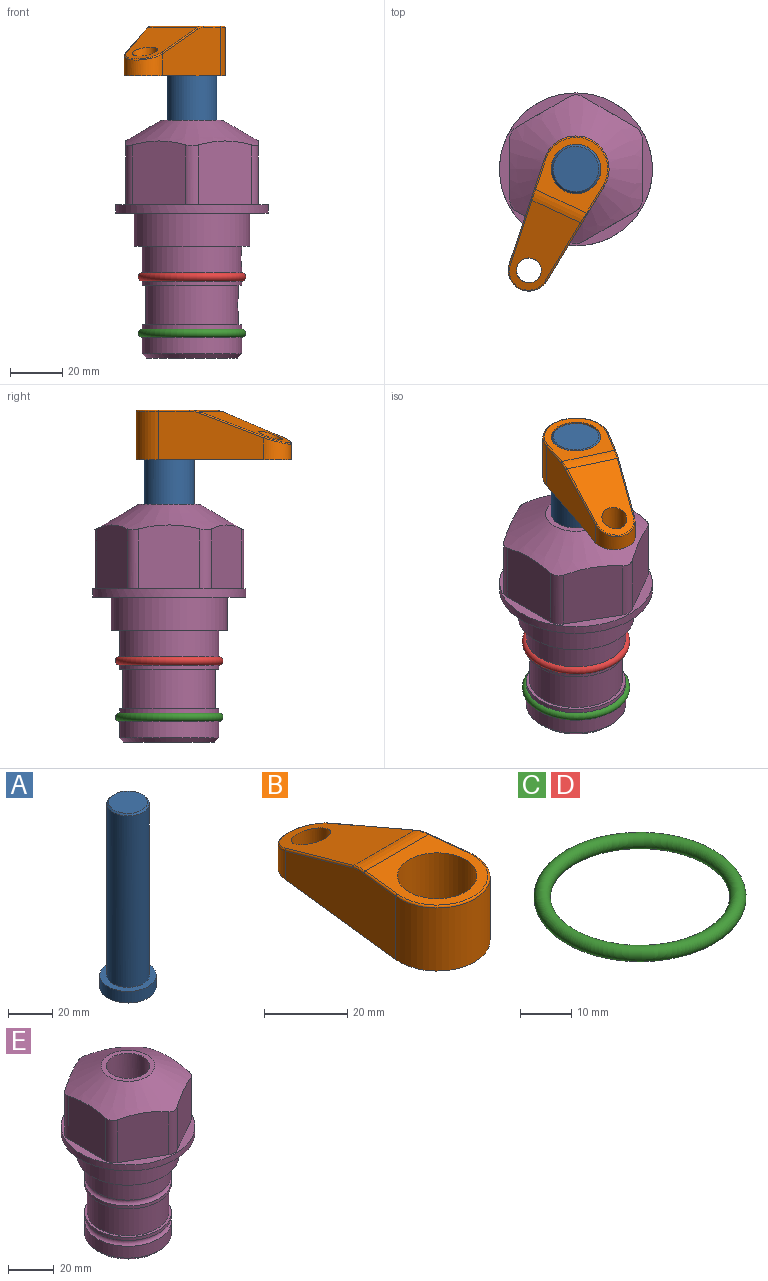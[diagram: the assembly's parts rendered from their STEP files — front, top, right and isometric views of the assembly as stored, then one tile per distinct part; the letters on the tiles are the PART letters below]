
ASSEMBLY  parts=5 mates=3
PART A: 6 faces, bbox 25.4x25.4x101.6 mm
  f0: plane 17.46x17.46mm, normal (0,0,1), area 239.5mm2, adj f5
  f1: plane 25.4x25.4mm, normal (0,0,-1), area 506.7mm2, adj f2
  f2: cylinder r=12.7mm len=25.4mm, axis (0,0,1), area 506.7mm2, adj f1,f3
  f3: plane 25.4x25.4mm, normal (0,0,1), area 221.7mm2, adj f2,f4
  f4: cylinder r=9.53mm len=94.46mm, axis (0,0,1), area 5653mm2, adj f3,f5
  f5: cone r=8.73mm half-angle=45deg, axis (0,0,-1), area 64.4mm2, adj f0,f4
PART B: 44 faces, bbox 27.5x64.5x19.1 mm
  f0: plane 2.3x0.95mm, normal (0,0,-1), area 1mm2, adj f25,f30,f34
  f1: plane 63.5x25.4mm, normal (0,0,-1), area 561.7mm2, adj f2,f3,f4,f5,f6,f7,f19,f20
  f2: cylinder r=12.7mm len=25.4mm, axis (0,0,-1), area 792.2mm2, adj f1,f3,f5,f13
  f3: plane 42.33x18.54mm, normal (0.99,0.11,0), area 647mm2, adj f1,f2,f4,f11,f12,f14
  f4: cylinder r=7.94mm len=15.78mm, axis (0,0,-1), area 158.6mm2, adj f1,f3,f5,f16
  f5: plane 42.33x18.54mm, normal (-0.99,0.11,0), area 647mm2, adj f1,f2,f4,f15,f17,f18
  f6: cylinder r=9.53mm len=19.05mm, axis (0,0,-1), area 1140.1mm2, adj f1,f8
  f7: cylinder r=4.76mm len=10.98mm, axis (0,0,-1), area 276.1mm2, adj f1,f9
  f8: plane 25.83x24.38mm, normal (0,0,1), area 262.2mm2, adj f6,f10,f11,f13,f15
  f9: plane 32.49x20.55mm, normal (0,0.34,0.94), area 489.9mm2, adj f7,f10,f14,f16,f18
  f10: cylinder r=12.7mm len=21.49mm, axis (-1,0,0), area 93.2mm2, adj f8,f9,f12,f17
  f11: cylinder r=0.51mm len=12.34mm, axis (0.11,-0.99,0), area 9.9mm2, adj f3,f8,f12,f13
  f12: bspline ~7.62x1.64mm, area 3.5mm2, adj f3,f10,f11,f14
  f13: torus R=12.19mm, axis (0,0,1), area 33.6mm2, adj f2,f8,f11,f15
  f14: cylinder r=0.51mm len=26.01mm, axis (0.1,-0.93,0.34), area 21.6mm2, adj f3,f9,f12,f16
  f15: cylinder r=0.51mm len=12.34mm, axis (0.11,0.99,0), area 9.9mm2, adj f5,f8,f13,f17
  f16: bspline ~15.78x7.05mm, area 15.7mm2, adj f4,f9,f14,f18
  f17: bspline ~7.62x1.64mm, area 3.5mm2, adj f5,f10,f15,f18
  f18: cylinder r=0.51mm len=26.01mm, axis (0.1,0.93,-0.34), area 21.6mm2, adj f5,f9,f16,f17
  f19: plane 21.6x14.29mm, normal (-0.99,-0.11,0), area 242.6mm2, adj f1,f26,f28,f34,f36,f38
  f20: plane 21.6x14.29mm, normal (0.99,-0.11,0), area 242.6mm2, adj f1,f27,f29,f37,f39,f41
  f21: cylinder r=12.7mm len=14.29mm, axis (0,0,-1), area 173.2mm2, adj f1,f26,f27,f30,f31,f33
  f22: cylinder r=7.94mm len=7.63mm, axis (0,0,-1), area 53.8mm2, adj f1,f28,f29,f42
  f23: plane 2.3x0.95mm, normal (0,0,-1), area 1mm2, adj f25,f33,f37
  f24: plane 17.94x12.32mm, normal (0,-0.34,-0.94), area 191.2mm2, adj f25,f38,f41,f42
  f25: cylinder r=9.53mm len=12.93mm, axis (-1,0,0), area 37.5mm2, adj f0,f23,f24,f31,f36,f39
  f26: cylinder r=1.59mm len=14.29mm, axis (0,0,-1), area 49mm2, adj f1,f19,f21,f32
  f27: cylinder r=1.59mm len=14.29mm, axis (0,0,-1), area 49mm2, adj f1,f20,f21,f35
  f28: cylinder r=1.59mm len=7.28mm, axis (0,0,-1), area 22.1mm2, adj f1,f19,f22,f40
  f29: cylinder r=1.59mm len=7.28mm, axis (0,0,-1), area 22.1mm2, adj f1,f20,f22,f43
  f30: torus R=14.29mm, axis (0,0,1), area 5.8mm2, adj f0,f21,f31,f32
  f31: bspline ~11.06x2.73mm, area 20.8mm2, adj f21,f25,f30,f33
  f32: sphere r=1.59mm, area 5.4mm2, adj f26,f30,f34
  f33: torus R=14.29mm, axis (0,0,1), area 5.8mm2, adj f21,f23,f31,f35
  f34: cylinder r=1.59mm len=1.68mm, axis (-0.11,0.99,0), area 2.4mm2, adj f0,f19,f32,f36
  f35: sphere r=1.59mm, area 5.4mm2, adj f27,f33,f37
  f36: bspline ~5.82x2.33mm, area 7.7mm2, adj f19,f25,f34,f38
  f37: cylinder r=1.59mm len=1.68mm, axis (0.11,0.99,0), area 2.4mm2, adj f20,f23,f35,f39
  f38: cylinder r=1.59mm len=18.33mm, axis (0.1,-0.93,0.34), area 46.7mm2, adj f19,f24,f36,f40
  f39: bspline ~5.82x2.33mm, area 7.7mm2, adj f20,f25,f37,f41
  f40: sphere r=1.59mm, area 3.6mm2, adj f28,f38,f42
  f41: cylinder r=1.59mm len=18.33mm, axis (0.1,0.93,-0.34), area 46.7mm2, adj f20,f24,f39,f43
  f42: bspline ~8.31x1.84mm, area 15.3mm2, adj f22,f24,f40,f43
  f43: sphere r=1.59mm, area 3.6mm2, adj f29,f41,f42
PART C: 1 faces, bbox 44.7x44.7x3.2 mm
  f0: torus R=19.05mm, axis (0,0,1), area 1193.9mm2
PART D: same geometry as C
PART E: 36 faces, bbox 58.7x58.7x91.2 mm
  f0: cylinder r=17.78mm len=35.56mm, axis (0,0,1), area 1670.8mm2, adj f23,f24,f31
  f1: cylinder r=19.05mm len=38.1mm, axis (0,0,1), area 1191.9mm2, adj f26,f27,f30
  f2: plane 58.66x58.66mm, normal (0,0,-1), area 1150.6mm2, adj f3,f28
  f3: cylinder r=29.33mm len=58.66mm, axis (0,0,-1), area 585.1mm2, adj f2,f4
  f4: plane 58.66x58.66mm, normal (0,0,1), area 475.9mm2, adj f3,f5,f6,f7,f8,f9,f10,f11
  f5: plane 24.5x20.32mm, normal (-0.5,0.87,0), area 562.8mm2, adj f4,f15,f16,f17
  f6: plane 24.5x20.32mm, normal (0.5,0.87,0), area 562.8mm2, adj f4,f14,f15,f17
  f7: plane 24.5x23.48mm, normal (1,0,0), area 562.8mm2, adj f4,f13,f14,f17
  f8: plane 24.5x20.32mm, normal (0.5,-0.87,0), area 562.8mm2, adj f4,f12,f13,f17
  f9: plane 24.5x20.32mm, normal (-0.5,-0.87,0), area 562.8mm2, adj f4,f11,f12,f17
  f10: plane 24.5x23.48mm, normal (-1,0,0), area 562.8mm2, adj f4,f11,f16,f17
  f11: cylinder r=5.08mm len=23.01mm, axis (0,0,-1), area 121.2mm2, adj f4,f9,f10,f17
  f12: cylinder r=5.08mm len=23.01mm, axis (0,0,-1), area 121.2mm2, adj f4,f8,f9,f17
  f13: cylinder r=5.08mm len=23.01mm, axis (0,0,-1), area 121.2mm2, adj f4,f7,f8,f17
  f14: cylinder r=5.08mm len=23.01mm, axis (0,0,-1), area 121.2mm2, adj f4,f6,f7,f17
  f15: cylinder r=5.08mm len=23.01mm, axis (0,0,-1), area 121.2mm2, adj f4,f5,f6,f17
  f16: cylinder r=5.08mm len=23.01mm, axis (0,0,-1), area 121.2mm2, adj f4,f5,f10,f17
  f17: cone r=11.73mm half-angle=60deg, axis (0,0,-1), area 2071.8mm2, adj f5,f6,f7,f8,f9,f10,f11,f12
  f18: plane 23.46x23.46mm, normal (0,0,1), area 147.4mm2, adj f17,f35
  f19: plane 34.93x34.93mm, normal (0,0,-1), area 958mm2, adj f29
  f20: cylinder r=19.05mm len=38.1mm, axis (0,0,1), area 760.1mm2, adj f21,f29
  f21: torus R=19.05mm, axis (0,0,1), area 565.3mm2, adj f20,f22
  f22: cylinder r=19.05mm len=38.1mm, axis (0,0,1), area 190mm2, adj f21,f23
  f23: plane 38.1x38.1mm, normal (0,0,1), area 146.9mm2, adj f0,f22
  f24: plane 38.1x38.1mm, normal (0,0,-1), area 146.9mm2, adj f0,f25
  f25: cylinder r=19.05mm len=38.1mm, axis (0,0,1), area 190mm2, adj f24,f26
  f26: torus R=19.05mm, axis (0,0,1), area 565.3mm2, adj f1,f25
  f27: plane 44.45x44.45mm, normal (0,0,-1), area 411.7mm2, adj f1,f28
  f28: cylinder r=22.23mm len=44.45mm, axis (0,0,1), area 1773.5mm2, adj f2,f27
  f29: cone r=19.05mm half-angle=45deg, axis (0,0,1), area 257.5mm2, adj f19,f20
  f30: cylinder r=3.17mm len=6.75mm, axis (-1,0,0), area 128mm2, adj f1,f33
  f31: cylinder r=3.17mm len=6.35mm, axis (-1,0,0), area 102.5mm2, adj f0,f33
  f32: plane 25.4x25.4mm, normal (0,0,1), area 506.7mm2, adj f33
  f33: cylinder r=12.7mm len=66.42mm, axis (0,0,-1), area 5236.2mm2, adj f30,f31,f32,f34
  f34: cone r=9.53mm half-angle=30deg, axis (0,0,-1), area 443.4mm2, adj f33,f35
  f35: cylinder r=9.53mm len=19.05mm, axis (0,0,-1), area 849mm2, adj f18,f34
PLACE A rot(axis=(0,0,-1),114.9deg) t=(0,0,-1.89)mm
PLACE B rot(axis=(0,0,1),155.1deg) t=(0,0,52.72)mm
PLACE C t=(0,0,-21.59)mm
PLACE D at identity
PLACE E at identity fixed
MATE fastened C.f0 <-> E.f0  axis (0,0,1) through (0,0,-46.1)mm
MATE cylindrical A.f2 <-> E.f0  axis (0,0,1) through (0,0,23.75)mm
MATE fastened B.f2 <-> A.f2  axis (0,0,1) through (0,0,71.77)mm
